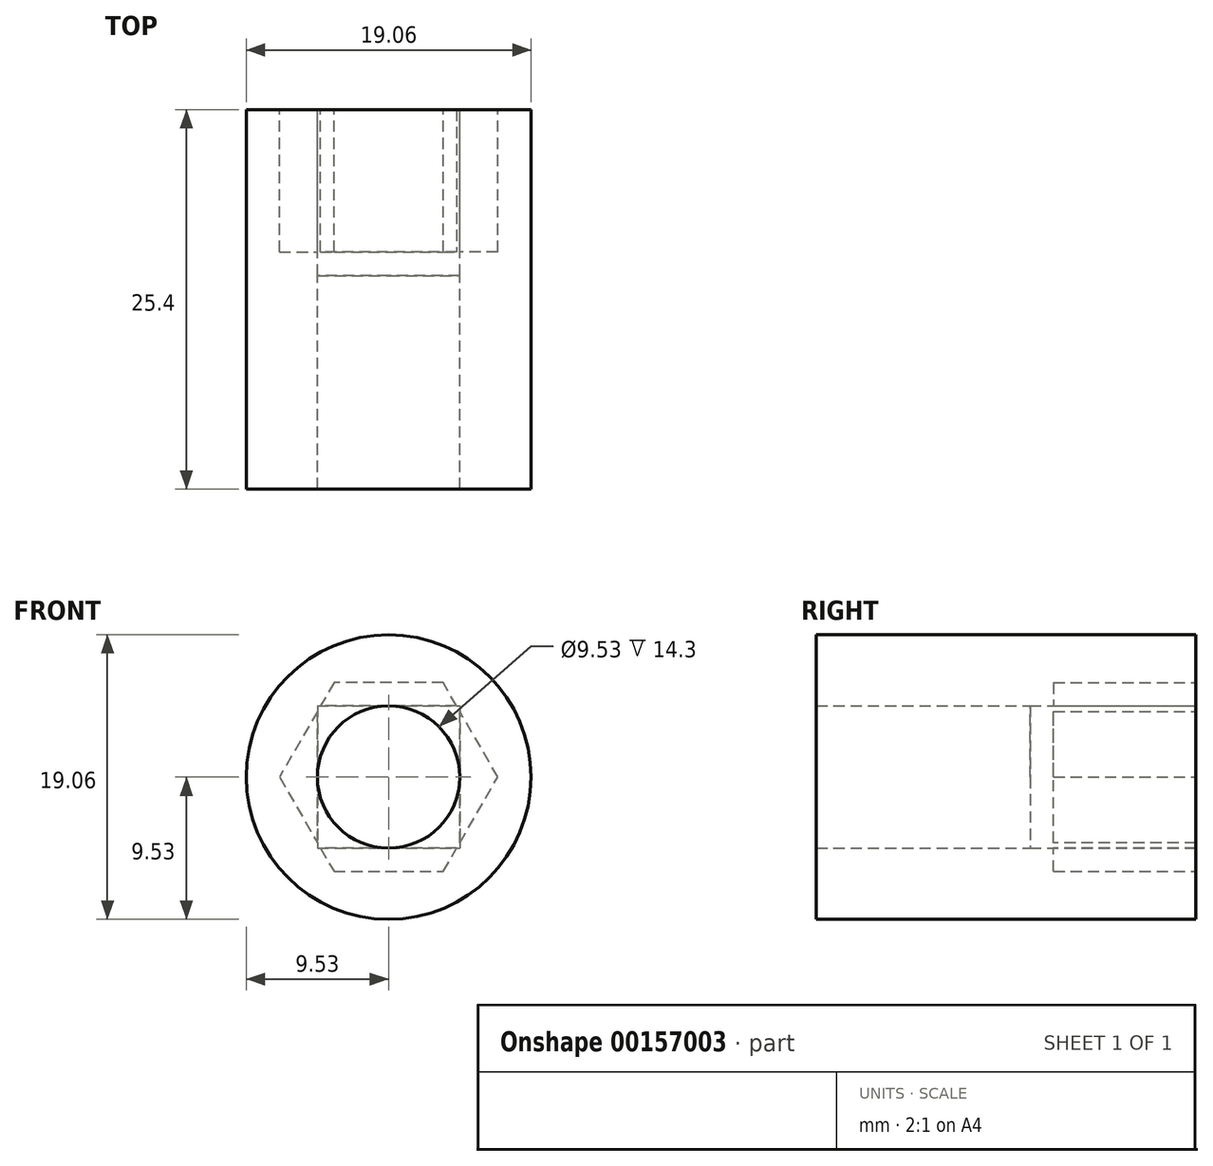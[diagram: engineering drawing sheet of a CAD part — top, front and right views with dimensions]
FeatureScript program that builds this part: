
annotation { "Feature Type Name" : "Feature", "Feature Type Description" : "" }
export const myFeature = defineFeature(function(context is Context, id is Id, definition is map)
    precondition{}
    {
        {
            var Q0;
            Q0=qCreatedBy(makeId("Front.planeOp"),FACE);
            var sketch = newSketch(context, id + "F0", { "sketchPlane" : qUnion([Q0])});
            skCircle(sketch, "E0", {"center": v(0, 0) * mm, "radius": 9.53 * mm});
            skSolve(sketch);
        }
        {
            var Q0;
            Q0=makeQuery(id+"F0.imprint","IMPRINT",FACE,{"disambiguationData":[TD([[makeQuery(id+"F0.imprint","IMPRINT",EDGE,{"derivedFrom":sQuery(id+"F0.wireOp",EDGE,"E0")}),1.0]])]});
            extrude(context, id + "F1", {"entities" : qUnion([Q0]), "depth" : 25.4 * mm});
        }
        {
            var Q0;
            Q0=qCreatedBy(makeId("Front.planeOp"),FACE);
            var sketch = newSketch(context, id + "F2", { "sketchPlane" : qUnion([Q0])});
            skLineSegment(sketch, "E1.bottom", {"start": v(-4.76, 4.76) * mm, "end": v(4.76, 4.76) * mm});
            skLineSegment(sketch, "E1.top", {"start": v(-4.76, -4.76) * mm, "end": v(4.76, -4.76) * mm});
            skLineSegment(sketch, "E1.left", {"start": v(-4.76, 4.76) * mm, "end": v(-4.76, -4.76) * mm});
            skLineSegment(sketch, "E1.right", {"start": v(4.76, 4.76) * mm, "end": v(4.76, -4.76) * mm});
            skPoint(sketch, "E1.middle", {"position": v(0, 0) * mm});
            skCircle(sketch, "E2", {"center": v(0, 0) * mm, "radius": 4.76 * mm});
            skSolve(sketch);
        }
        {
            var Q0;
            {var subQ0=sQuery(id+"F2.wireOp",EDGE,"E2");var subQ1=makeQuery(id+"F2.imprint","INTERSECT",VERTEX,{"derivedFrom":[sQuery(id+"F2.wireOp",EDGE,"E1.bottom"),subQ0]});Q0=makeQuery(id+"F2.imprint","IMPRINT",FACE,{"disambiguationData":[TD([[makeQuery(id+"F2.imprint","IMPRINT",EDGE,{"disambiguationData":[TD([[subQ1,1.0]])],"derivedFrom":subQ0}),1.0]])]});}
            extrude(context, id + "F3", {"entities" : qUnion([Q0]), "operationType" : NewBodyOperationType.REMOVE, "endBound" : BoundingType.THROUGH_ALL, "depth" : 25.4 * mm});
        }
        {
            var Q0;
            Q0 = qSketchRegion(id + "F2", true);
            extrude(context, id + "F4", {"entities" : qUnion([Q0]), "operationType" : NewBodyOperationType.REMOVE, "depth" : 11.1 * mm});
        }
        {
            var Q0;
            Q0=makeQuery(id+"F1.opExtrude","CAP_FACE",FACE,{"disambiguationData":[OSD([sQuery(id+"F0.wireOp",EDGE,"E0")])],"isStart":true});
            var sketch = newSketch(context, id + "F5", { "sketchPlane" : qUnion([Q0])});
            skCircle(sketch, "E3.cCircle", {"center": v(0, 0) * mm, "radius": 6.32 * mm, "construction": true});
            skLineSegment(sketch, "E3.0", {"start": v(-3.65, 6.32) * mm, "end": v(3.65, 6.32) * mm});
            skLineSegment(sketch, "E3.1", {"start": v(3.65, 6.32) * mm, "end": v(7.3, 0) * mm});
            skLineSegment(sketch, "E3.2", {"start": v(7.3, 0) * mm, "end": v(3.65, -6.32) * mm});
            skLineSegment(sketch, "E3.3", {"start": v(3.65, -6.32) * mm, "end": v(-3.65, -6.32) * mm});
            skLineSegment(sketch, "E3.4", {"start": v(-3.65, -6.32) * mm, "end": v(-7.3, 0) * mm});
            skLineSegment(sketch, "E3.5", {"start": v(-7.3, 0) * mm, "end": v(-3.65, 6.32) * mm});
            skPoint(sketch, "E3.0.midPoint", {"position": v(0, 6.32) * mm});
            skSolve(sketch);
        }
        {
            var Q0;
            Q0 = qSketchRegion(id + "F5", true);
            extrude(context, id + "F6", {"entities" : qUnion([Q0]), "operationType" : NewBodyOperationType.REMOVE, "oppositeDirection" : true, "depth" : 9.52 * mm});
        }
    });
